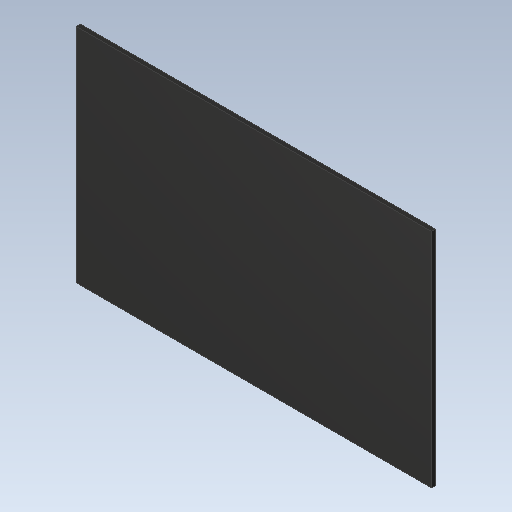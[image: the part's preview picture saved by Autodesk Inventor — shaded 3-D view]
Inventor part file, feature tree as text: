
AUTODESK INVENTOR PART (.ipt)
format: ipt  version: 2020 (Build 240168000, 168)  size: 85,504 bytes
history: imported  units: in
note: dims shown in document units (in); Inventor stores cm internally (conversion verified against a paired STEP export)
features: imported_body x1
ambient origin geometry x8: Origin, YZ Plane, XZ Plane, XY Plane, X Axis, Y Axis, Z Axis, Center Point
bodies: Solid1 (imported_parasolid), Body1 (imported_parasolid)
feature tree (1):
  imported_body  NMx_Import_Brep_tag  [imported B-rep: ~6 faces, bbox_mm=[8.8, 5.5, 0.1]]
